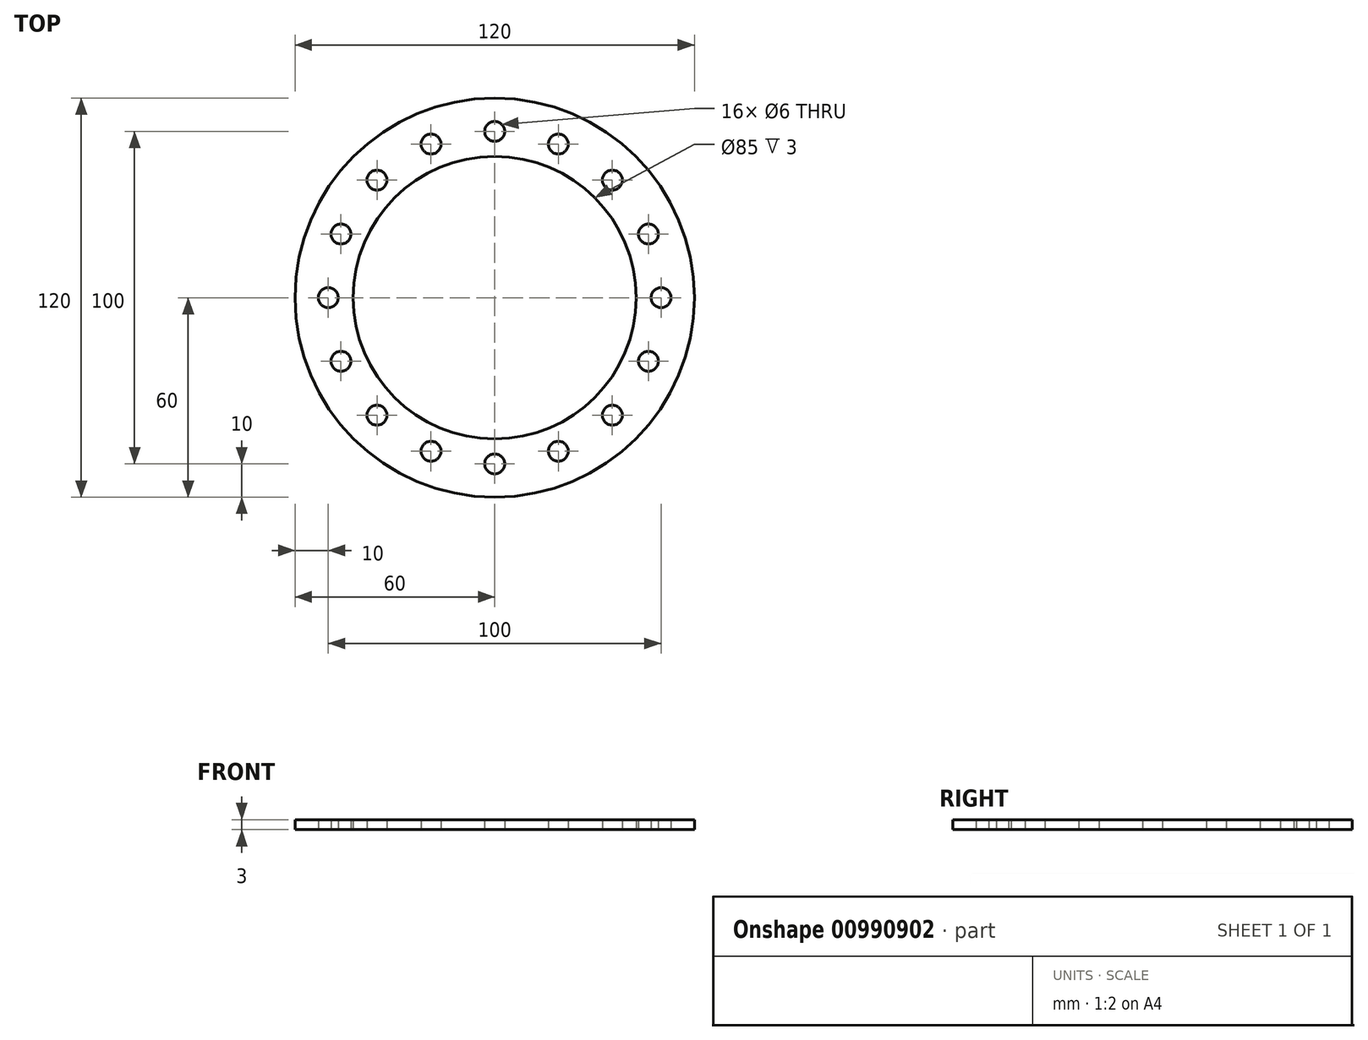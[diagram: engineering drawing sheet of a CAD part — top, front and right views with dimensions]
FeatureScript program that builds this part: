
annotation { "Feature Type Name" : "Feature", "Feature Type Description" : "" }
export const myFeature = defineFeature(function(context is Context, id is Id, definition is map)
    precondition{}
    {
        {
            var Q0;
            Q0=qCreatedBy(makeId("Top.planeOp"),FACE);
            var sketch = newSketch(context, id + "F0", { "sketchPlane" : qUnion([Q0])});
            skCircle(sketch, "E0", {"center": v(0, 0) * mm, "radius": 60 * mm});
            skCircle(sketch, "E1", {"center": v(0, 0) * mm, "radius": 42.5 * mm});
            skCircle(sketch, "E2", {"center": v(0, 0) * mm, "radius": 50 * mm, "construction": true});
            skCircle(sketch, "E3", {"center": v(0, 50) * mm, "radius": 3 * mm});
            skCircle(sketch, "E4.1.0", {"center": v(-19.13, 46.2) * mm, "radius": 3 * mm});
            skCircle(sketch, "E4.2.0", {"center": v(-35.36, 35.36) * mm, "radius": 3 * mm});
            skCircle(sketch, "E4.3.0", {"center": v(-46.2, 19.13) * mm, "radius": 3 * mm});
            skCircle(sketch, "E4.4.0", {"center": v(-50, 0) * mm, "radius": 3 * mm});
            skCircle(sketch, "E4.5.0", {"center": v(-46.2, -19.13) * mm, "radius": 3 * mm});
            skCircle(sketch, "E4.6.0", {"center": v(-35.36, -35.36) * mm, "radius": 3 * mm});
            skCircle(sketch, "E4.7.0", {"center": v(-19.13, -46.2) * mm, "radius": 3 * mm});
            skCircle(sketch, "E4.8.0", {"center": v(0, -50) * mm, "radius": 3 * mm});
            skCircle(sketch, "E4.9.0", {"center": v(19.13, -46.2) * mm, "radius": 3 * mm});
            skCircle(sketch, "E4.10.0", {"center": v(35.36, -35.36) * mm, "radius": 3 * mm});
            skCircle(sketch, "E4.11.0", {"center": v(46.2, -19.13) * mm, "radius": 3 * mm});
            skCircle(sketch, "E4.12.0", {"center": v(50, 0) * mm, "radius": 3 * mm});
            skCircle(sketch, "E4.13.0", {"center": v(46.2, 19.13) * mm, "radius": 3 * mm});
            skCircle(sketch, "E4.14.0", {"center": v(35.36, 35.36) * mm, "radius": 3 * mm});
            skCircle(sketch, "E4.15.0", {"center": v(19.13, 46.2) * mm, "radius": 3 * mm});
            skSolve(sketch);
        }
        {
            var Q0;
            Q0=makeQuery(id+"F0.imprint","IMPRINT",FACE,{"disambiguationData":[TD([[makeQuery(id+"F0.imprint","IMPRINT",EDGE,{"derivedFrom":sQuery(id+"F0.wireOp",EDGE,"E0")}),1.0]])]});
            extrude(context, id + "F1", {"entities" : qUnion([Q0]), "depth" : 3 * mm, "offsetDistance" : 25 * mm});
        }
    });
